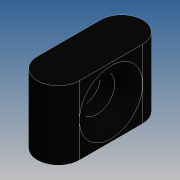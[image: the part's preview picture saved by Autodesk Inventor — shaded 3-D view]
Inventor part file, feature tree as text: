
AUTODESK INVENTOR PART (.ipt)
format: ipt  version: 2019 (Build 230136000, 136)  size: 258,560 bytes
history: native  units: mm
features: fillet x2, sketch x2, extrude x1, mirror x1, hole x1
ambient origin geometry x8: Origin, YZ Plane, XZ Plane, XY Plane, X Axis, Y Axis, Z Axis, Center Point
bodies: Solid1 (feature_tree)
feature tree (7):
  extrude  "Extrusion1"  Depth=9.8mm
  fillet  "Fillet1"  Radius=9.8mm
  mirror  "Mirror1"
  hole  "Hole1"  [1 undecoded]
  fillet  "Fillet2"  [1 undecoded]
  sketch  "Sketch1"  dims[d0=6.0mm d1=7.5mm d2=9.8mm d3=0.0mm]
  sketch  "Sketch2"  dims[d4=3.0mm d5=5.0mm d6=6.0mm d7=4.0mm d8=2.0mm d9=90.0deg d10=8.0mm d11=20.594885mm d12=2.0mm]
note: 2 required parameter values undecoded (feature->parameter linkage not recoverable at this tier; creation-order binding heuristic only, values carry confidence <= 0.55)
